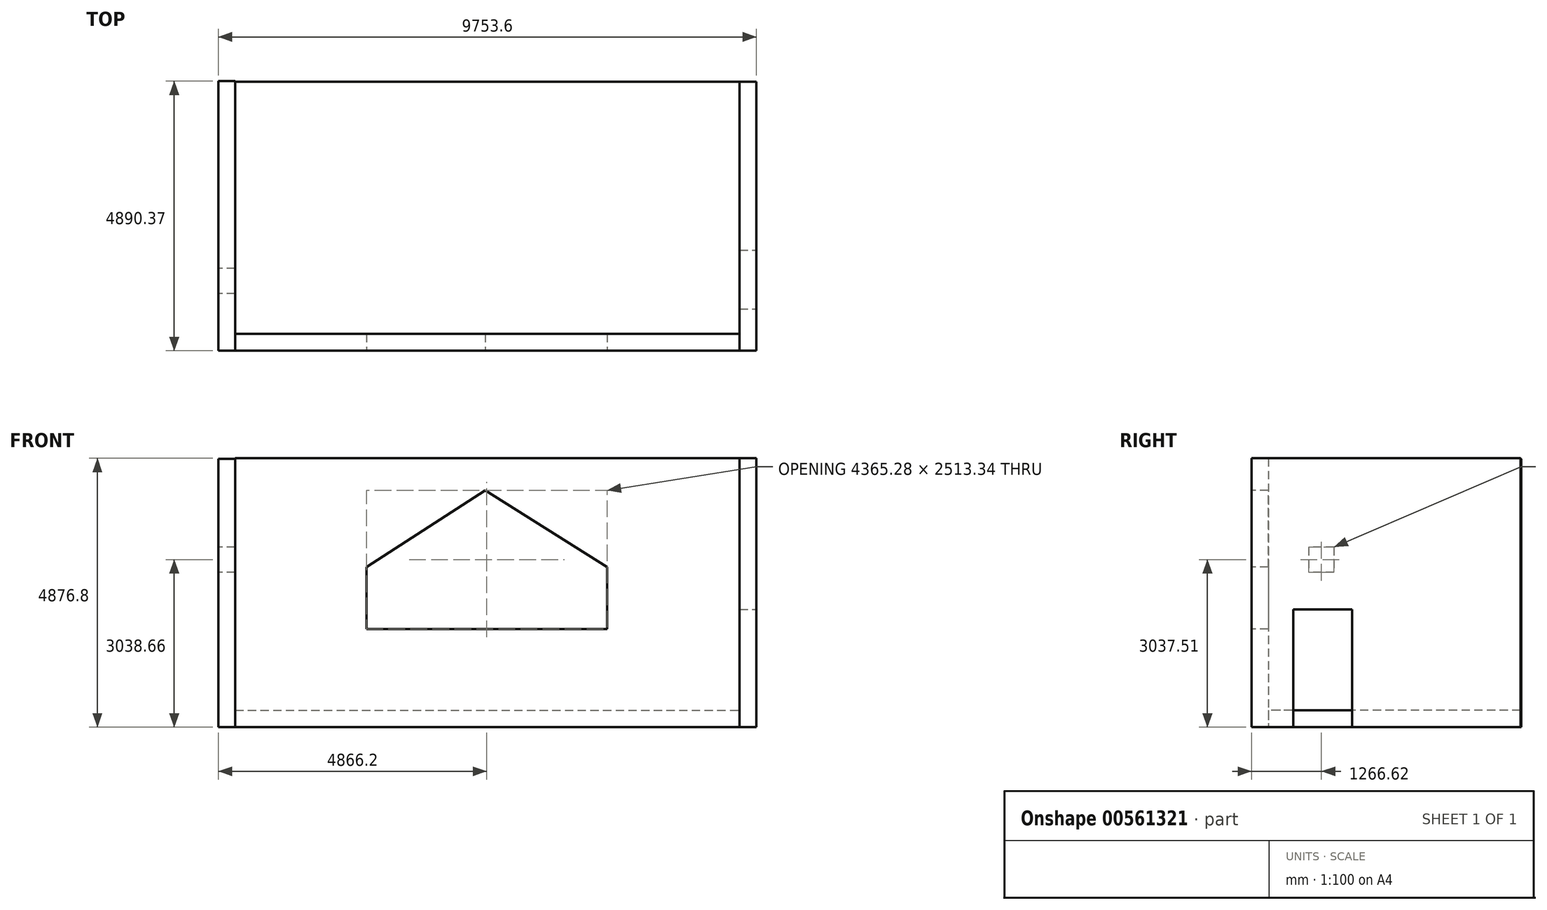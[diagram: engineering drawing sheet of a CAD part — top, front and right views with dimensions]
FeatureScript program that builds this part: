
annotation { "Feature Type Name" : "Feature", "Feature Type Description" : "" }
export const myFeature = defineFeature(function(context is Context, id is Id, definition is map)
    precondition{}
    {
        {
            var Q0;
            Q0=qCreatedBy(makeId("Top.planeOp"),FACE);
            var sketch = newSketch(context, id + "F0", { "sketchPlane" : qUnion([Q0])});
            skLineSegment(sketch, "E0.bottom", {"start": v(-3176.14, 2298.66) * mm, "end": v(5967.86, 2298.66) * mm});
            skLineSegment(sketch, "E0.top", {"start": v(-3176.14, -2273.34) * mm, "end": v(5967.86, -2273.34) * mm});
            skLineSegment(sketch, "E0.left", {"start": v(-3176.14, 2298.66) * mm, "end": v(-3176.14, -2273.34) * mm});
            skLineSegment(sketch, "E0.right", {"start": v(5967.86, 2298.66) * mm, "end": v(5967.86, -2273.34) * mm});
            skSolve(sketch);
        }
        {
            var Q0;
            Q0 = qSketchRegion(id + "F0", true);
            extrude(context, id + "F1", {"entities" : qUnion([Q0]), "depth" : 304.8 * mm, "offsetDistance" : 30.48 * mm});
        }
        {
            var Q0;
            Q0=makeQuery(id+"F1.opExtrude","SWEPT_FACE",FACE,{"disambiguationData":[OSD([sQuery(id+"F0.wireOp",EDGE,"E0.top")])]});
            var sketch = newSketch(context, id + "F2", { "sketchPlane" : qUnion([Q0])});
            skLineSegment(sketch, "E1.bottom", {"start": v(-3176.14, 0) * mm, "end": v(5967.86, 0) * mm});
            skLineSegment(sketch, "E1.top", {"start": v(-3176.14, 0) * mm, "end": v(5967.86, 0) * mm});
            skLineSegment(sketch, "E1.left", {"start": v(-3176.14, 0) * mm, "end": v(-3176.14, 0) * mm});
            skLineSegment(sketch, "E1.right", {"start": v(5967.86, 0) * mm, "end": v(5967.86, 0) * mm});
            skLineSegment(sketch, "E2.top", {"start": v(-3176.14, 4876.8) * mm, "end": v(5967.86, 4876.8) * mm});
            skLineSegment(sketch, "E2.left", {"start": v(-3176.14, 0) * mm, "end": v(-3176.14, 4876.8) * mm});
            skLineSegment(sketch, "E2.right", {"start": v(5967.86, 0) * mm, "end": v(5967.86, 4876.8) * mm});
            skSolve(sketch);
        }
        {
            var Q0;
            Q0 = qSketchRegion(id + "F2", true);
            extrude(context, id + "F3", {"entities" : qUnion([Q0]), "depth" : 304.8 * mm, "offsetDistance" : 30.48 * mm});
        }
        {
            var Q0;
            Q0=makeQuery(id+"F3.boolean.opBoolean","MERGE",FACE,{"derivedFrom":[makeQuery(id+"F1.opExtrude","SWEPT_FACE",FACE,{"disambiguationData":[OSD([sQuery(id+"F0.wireOp",EDGE,"E0.right")])]}),makeQuery(id+"F3.opExtrude","SWEPT_FACE",FACE,{"disambiguationData":[OSD([sQuery(id+"F2.wireOp",EDGE,"E2.right")])]})]});
            var sketch = newSketch(context, id + "F4", { "sketchPlane" : qUnion([Q0])});
            skLineSegment(sketch, "E3.bottom", {"start": v(-2578.14, 0) * mm, "end": v(2298.66, 0) * mm});
            skLineSegment(sketch, "E3.top", {"start": v(-2578.14, 4876.8) * mm, "end": v(2298.66, 4876.8) * mm});
            skLineSegment(sketch, "E3.left", {"start": v(-2578.14, 0) * mm, "end": v(-2578.14, 4876.8) * mm});
            skLineSegment(sketch, "E3.right", {"start": v(2298.66, 0) * mm, "end": v(2298.66, 4876.8) * mm});
            skSolve(sketch);
        }
        {
            var Q0;
            Q0 = qSketchRegion(id + "F4", true);
            extrude(context, id + "F5", {"entities" : qUnion([Q0]), "depth" : 304.8 * mm, "offsetDistance" : 30.48 * mm});
        }
        {
            var Q0;
            Q0=makeQuery(id+"F3.boolean.opBoolean","MERGE",FACE,{"derivedFrom":[makeQuery(id+"F1.opExtrude","SWEPT_FACE",FACE,{"disambiguationData":[OSD([sQuery(id+"F0.wireOp",EDGE,"E0.left")])]}),makeQuery(id+"F3.opExtrude","SWEPT_FACE",FACE,{"disambiguationData":[OSD([sQuery(id+"F2.wireOp",EDGE,"E2.left")])]})]});
            var sketch = newSketch(context, id + "F6", { "sketchPlane" : qUnion([Q0])});
            skLineSegment(sketch, "E4.bottom", {"start": v(-2312.23, 4867.2) * mm, "end": v(2578.14, 4867.2) * mm});
            skLineSegment(sketch, "E4.top", {"start": v(-2312.23, 0) * mm, "end": v(2578.14, 0) * mm});
            skLineSegment(sketch, "E4.left", {"start": v(-2312.23, 4867.2) * mm, "end": v(-2312.23, 0) * mm});
            skLineSegment(sketch, "E4.right", {"start": v(2578.14, 4867.2) * mm, "end": v(2578.14, 0) * mm});
            skSolve(sketch);
        }
        {
            var Q0;
            Q0 = qSketchRegion(id + "F6", true);
            extrude(context, id + "F7", {"entities" : qUnion([Q0]), "depth" : 304.8 * mm, "offsetDistance" : 30.48 * mm});
        }
        {
            var Q0;
            Q0=makeQuery(id+"F7.opExtrude","CAP_FACE",FACE,{"disambiguationData":[OSD([sQuery(id+"F6.wireOp",EDGE,"E4.bottom"),sQuery(id+"F6.wireOp",EDGE,"E4.top"),sQuery(id+"F6.wireOp",EDGE,"E4.left"),sQuery(id+"F6.wireOp",EDGE,"E4.right")])],"isStart":false});
            var sketch = newSketch(context, id + "F8", { "sketchPlane" : qUnion([Q0])});
            skLineSegment(sketch, "E5.bottom", {"start": v(1082.92, 3266.1) * mm, "end": v(1540.12, 3266.1) * mm});
            skLineSegment(sketch, "E5.top", {"start": v(1082.92, 2808.9) * mm, "end": v(1540.12, 2808.9) * mm});
            skLineSegment(sketch, "E5.left", {"start": v(1082.92, 3266.1) * mm, "end": v(1082.92, 2808.9) * mm});
            skLineSegment(sketch, "E5.right", {"start": v(1540.12, 3266.1) * mm, "end": v(1540.12, 2808.9) * mm});
            skSolve(sketch);
        }
        {
            var Q0;
            Q0 = qSketchRegion(id + "F8", true);
            extrude(context, id + "F9", {"entities" : qUnion([Q0]), "operationType" : NewBodyOperationType.REMOVE, "oppositeDirection" : true, "depth" : 609.6 * mm, "offsetDistance" : 30.48 * mm});
        }
        {
            var Q0;
            Q0=makeQuery(id+"F5.opExtrude","CAP_FACE",FACE,{"disambiguationData":[OSD([sQuery(id+"F4.wireOp",EDGE,"E3.bottom"),sQuery(id+"F4.wireOp",EDGE,"E3.top"),sQuery(id+"F4.wireOp",EDGE,"E3.left"),sQuery(id+"F4.wireOp",EDGE,"E3.right")])],"isStart":false});
            var sketch = newSketch(context, id + "F10", { "sketchPlane" : qUnion([Q0])});
            skLineSegment(sketch, "E6.bottom", {"start": v(-1821.3, 0) * mm, "end": v(-754.5, 0) * mm});
            skLineSegment(sketch, "E6.top", {"start": v(-1821.3, 2133.6) * mm, "end": v(-754.5, 2133.6) * mm});
            skLineSegment(sketch, "E6.left", {"start": v(-1821.3, 0) * mm, "end": v(-1821.3, 2133.6) * mm});
            skLineSegment(sketch, "E6.right", {"start": v(-754.5, 0) * mm, "end": v(-754.5, 2133.6) * mm});
            skSolve(sketch);
        }
        {
            var Q0;
            Q0 = qSketchRegion(id + "F10", true);
            extrude(context, id + "F11", {"entities" : qUnion([Q0]), "operationType" : NewBodyOperationType.REMOVE, "oppositeDirection" : true, "depth" : 304.8 * mm, "offsetDistance" : 30.48 * mm});
        }
        {
            var Q0;
            Q0=makeQuery(id+"F3.opExtrude","CAP_FACE",FACE,{"disambiguationData":[OSD([sQuery(id+"F2.wireOp",EDGE,"E1.bottom"),sQuery(id+"F2.wireOp",EDGE,"E2.top"),sQuery(id+"F2.wireOp",EDGE,"E2.left"),sQuery(id+"F2.wireOp",EDGE,"E2.right")])],"isStart":false});
            var sketch = newSketch(context, id + "F12", { "sketchPlane" : qUnion([Q0])});
            skLineSegment(sketch, "E7.bottom", {"start": v(-797.38, 2906.38) * mm, "end": v(1358.8, 2906.38) * mm});
            skLineSegment(sketch, "E7.top", {"start": v(-797.38, 1781.99) * mm, "end": v(1358.8, 1781.99) * mm});
            skLineSegment(sketch, "E7.left", {"start": v(-797.38, 2906.38) * mm, "end": v(-797.38, 1781.99) * mm});
            skLineSegment(sketch, "E7.right", {"start": v(1358.8, 2906.38) * mm, "end": v(1358.8, 1781.99) * mm});
            skLineSegment(sketch, "E8.bottom", {"start": v(1358.8, 2906.38) * mm, "end": v(3567.9, 2906.38) * mm});
            skLineSegment(sketch, "E8.top", {"start": v(1358.8, 1781.99) * mm, "end": v(3567.9, 1781.99) * mm});
            skLineSegment(sketch, "E8.right", {"start": v(3567.9, 2906.38) * mm, "end": v(3567.9, 1781.99) * mm});
            skLineSegment(sketch, "E9", {"start": v(-797.38, 2906.38) * mm, "end": v(1358.8, 4295.33) * mm});
            skLineSegment(sketch, "E10", {"start": v(1358.8, 4295.33) * mm, "end": v(3567.9, 2906.38) * mm});
            skSolve(sketch);
        }
        {
            var Q0;
            Q0 = qSketchRegion(id + "F12", true);
            extrude(context, id + "F13", {"entities" : qUnion([Q0]), "operationType" : NewBodyOperationType.REMOVE, "oppositeDirection" : true, "depth" : 304.8 * mm, "offsetDistance" : 30.48 * mm});
        }
    });
